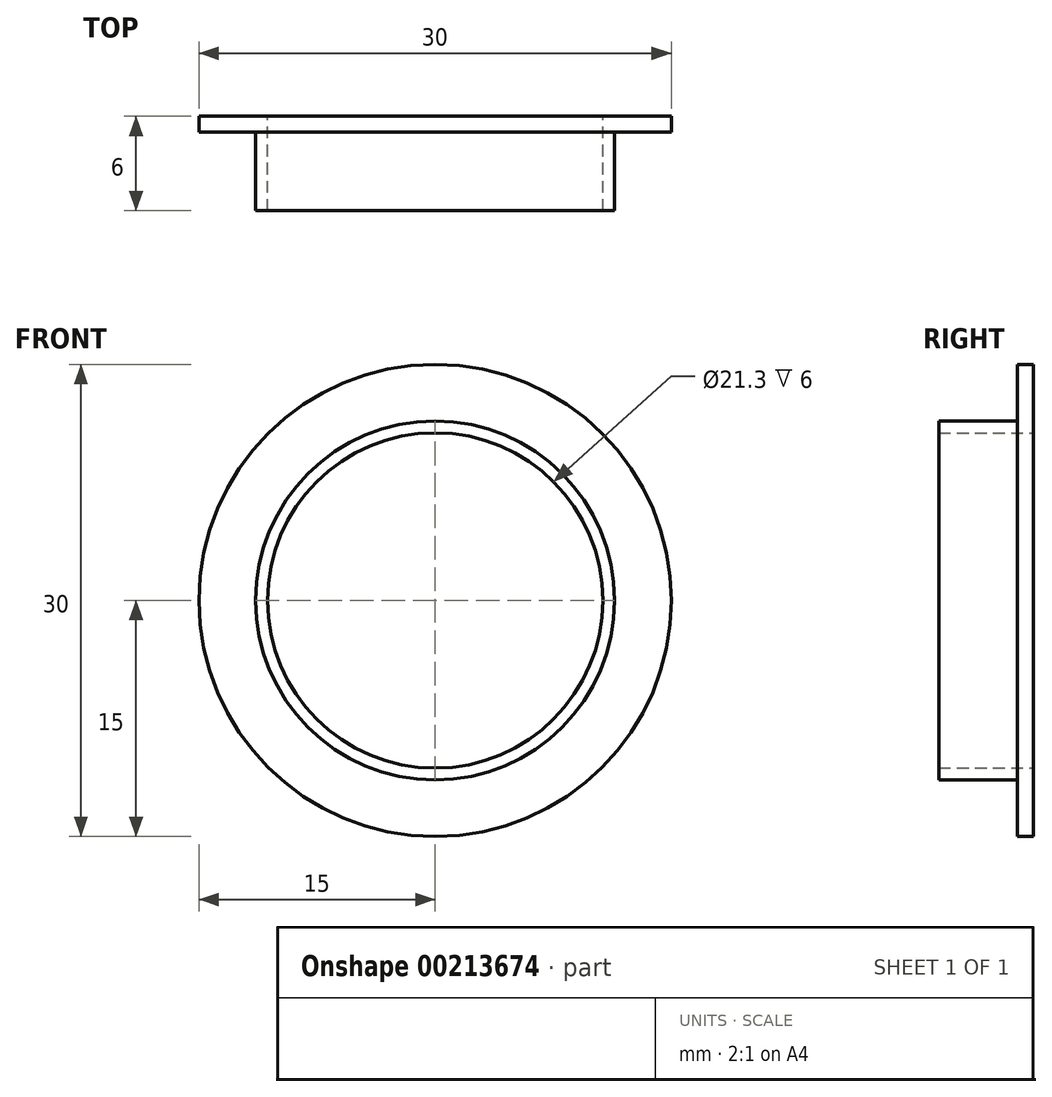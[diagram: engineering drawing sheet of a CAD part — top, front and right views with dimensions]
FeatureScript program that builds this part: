
annotation { "Feature Type Name" : "Feature", "Feature Type Description" : "" }
export const myFeature = defineFeature(function(context is Context, id is Id, definition is map)
    precondition{}
    {
        {
            var Q0;
            Q0=qCreatedBy(makeId("Front.planeOp"),FACE);
            var sketch = newSketch(context, id + "F0", { "sketchPlane" : qUnion([Q0])});
            skCircle(sketch, "E0", {"center": v(0, 0) * mm, "radius": 15 * mm});
            skCircle(sketch, "E1", {"center": v(0, 0) * mm, "radius": 10.65 * mm});
            skSolve(sketch);
        }
        {
            var Q0;
            Q0=makeQuery(id+"F0.imprint","IMPRINT",FACE,{"disambiguationData":[TD([[makeQuery(id+"F0.imprint","IMPRINT",EDGE,{"derivedFrom":sQuery(id+"F0.wireOp",EDGE,"E0")}),1.0]])]});
            extrude(context, id + "F1", {"entities" : qUnion([Q0]), "depth" : 1 * mm});
        }
        {
            var Q0;
            Q0=makeQuery(id+"F1.opExtrude","CAP_FACE",FACE,{"disambiguationData":[OSD([sQuery(id+"F0.wireOp",EDGE,"E0"),sQuery(id+"F0.wireOp",EDGE,"E1")])],"isStart":false});
            var sketch = newSketch(context, id + "F2", { "sketchPlane" : qUnion([Q0])});
            skCircle(sketch, "E2", {"center": v(0, 0) * mm, "radius": 11.4 * mm});
            skCircle(sketch, "E3", {"center": v(0, 0) * mm, "radius": 10.65 * mm});
            skSolve(sketch);
        }
        {
            var Q0;
            Q0=makeQuery(id+"F2.imprint","IMPRINT",FACE,{"disambiguationData":[TD([[makeQuery(id+"F2.imprint","IMPRINT",EDGE,{"derivedFrom":sQuery(id+"F2.wireOp",EDGE,"E2")}),1.0]])]});
            extrude(context, id + "F3", {"entities" : qUnion([Q0]), "operationType" : NewBodyOperationType.ADD, "depth" : 5 * mm});
        }
    });
